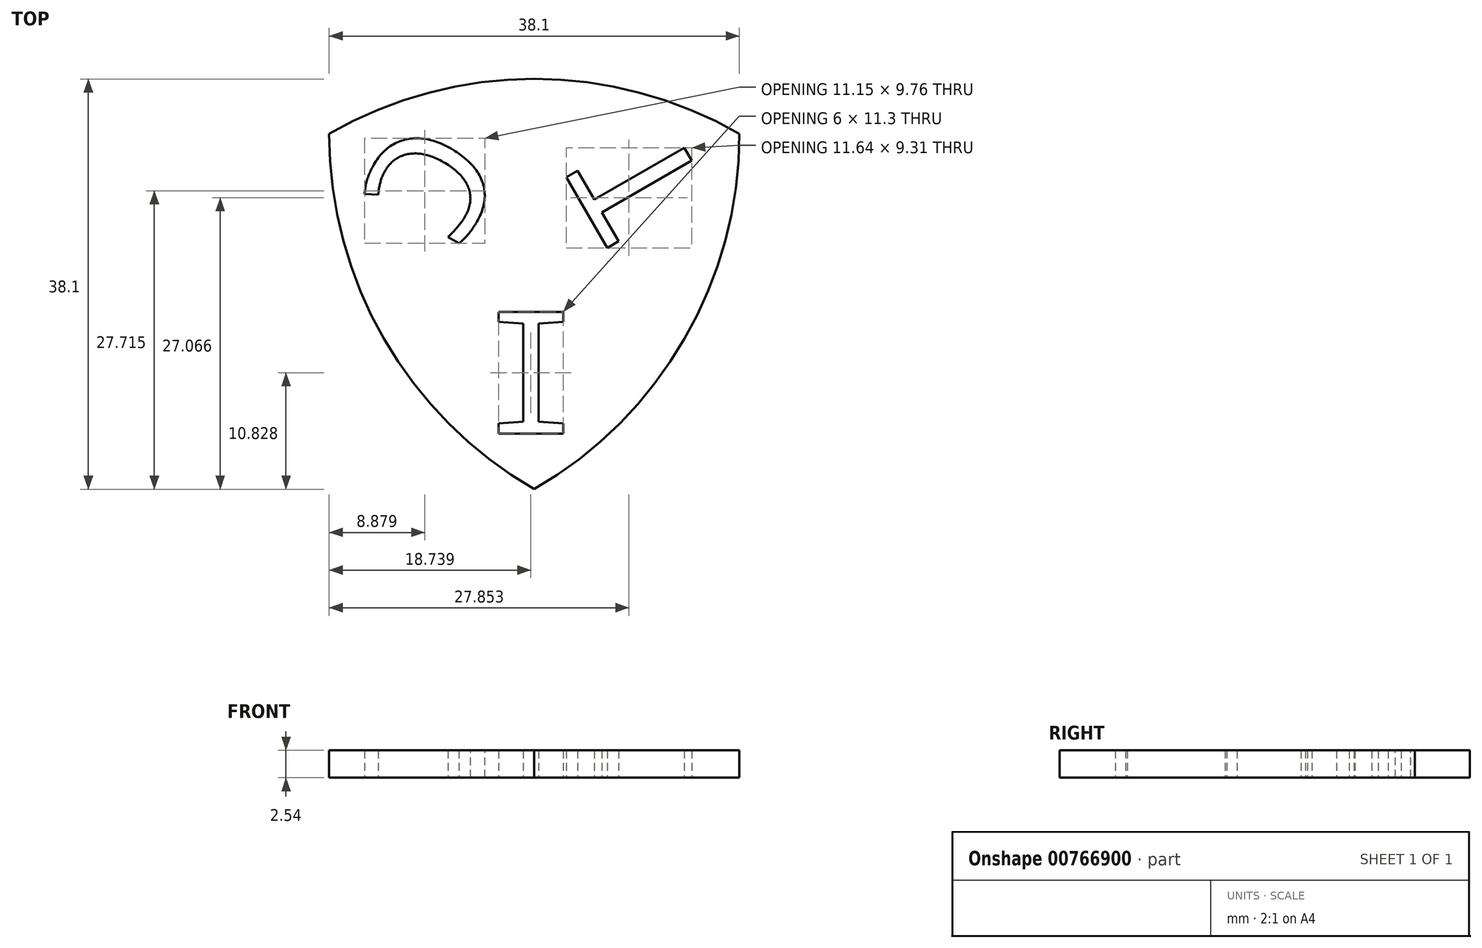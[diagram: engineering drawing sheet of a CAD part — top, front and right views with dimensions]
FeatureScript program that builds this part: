
annotation { "Feature Type Name" : "Feature", "Feature Type Description" : "" }
export const myFeature = defineFeature(function(context is Context, id is Id, definition is map)
    precondition{}
    {
        {
            var Q0;
            Q0=qCreatedBy(makeId("Top.planeOp"),FACE);
            var sketch = newSketch(context, id + "F0", { "sketchPlane" : qUnion([Q0])});
            skCircle(sketch, "E0", {"center": v(0, 0) * mm, "radius": 38.1 * mm});
            skSolve(sketch);
        }
        {
            var Q0;
            Q0=qCreatedBy(makeId("Top.planeOp"),FACE);
            var sketch = newSketch(context, id + "F1", { "sketchPlane" : qUnion([Q0])});
            skCircle(sketch, "E1", {"center": v(-38.1, 0) * mm, "radius": 38.1 * mm});
            skSolve(sketch);
        }
        {
            var Q0;
            Q0=qCreatedBy(makeId("Top.planeOp"),FACE);
            var sketch = newSketch(context, id + "F2", { "sketchPlane" : qUnion([Q0])});
            skCircle(sketch, "E2", {"center": v(-19.05, -33) * mm, "radius": 38.1 * mm});
            skSolve(sketch);
        }
        {
            var Q0;
            Q0=makeQuery(id+"F0.imprint","IMPRINT",FACE,{"disambiguationData":[TD([[makeQuery(id+"F0.imprint","IMPRINT",EDGE,{"derivedFrom":sQuery(id+"F0.wireOp",EDGE,"E0")}),1.0]])]});
            extrude(context, id + "F3", {"entities" : qUnion([Q0]), "depth" : 2.54 * mm, "offsetDistance" : 25.4 * mm});
        }
        {
            var Q0;
            Q0=makeQuery(id+"F1.imprint","IMPRINT",FACE,{"disambiguationData":[TD([[makeQuery(id+"F1.imprint","IMPRINT",EDGE,{"derivedFrom":sQuery(id+"F1.wireOp",EDGE,"E1")}),1.0]])]});
            extrude(context, id + "F4", {"entities" : qUnion([Q0]), "depth" : 2.54 * mm, "offsetDistance" : 25.4 * mm});
        }
        {
            var Q0;
            Q0=makeQuery(id+"F2.imprint","IMPRINT",FACE,{"disambiguationData":[TD([[makeQuery(id+"F2.imprint","IMPRINT",EDGE,{"derivedFrom":sQuery(id+"F2.wireOp",EDGE,"E2")}),1.0]])]});
            extrude(context, id + "F5", {"entities" : qUnion([Q0]), "depth" : 2.54 * mm, "offsetDistance" : 25.4 * mm});
        }
        {
            var Q0;
            Q0=makeQuery(id+"F4.opExtrude","SWEPT_BODY",BODY,{"disambiguationData":[OSD([sQuery(id+"F1.wireOp",EDGE,"E1")])]});
            var Q1;
            Q1=makeQuery(id+"F3.opExtrude","SWEPT_BODY",BODY,{"disambiguationData":[OSD([sQuery(id+"F0.wireOp",EDGE,"E0")])]});
            var Q2;
            Q2=makeQuery(id+"F5.opExtrude","SWEPT_BODY",BODY,{"disambiguationData":[OSD([sQuery(id+"F2.wireOp",EDGE,"E2")])]});
            booleanBodies(context, id + "F6", {"operationType" : BooleanOperationType.INTERSECTION, "tools" : qUnion([Q0, Q1, Q2])});
        }
        {
            var Q0;
            Q0=makeQuery(id+"F4.opExtrude","CAP_FACE",FACE,{"disambiguationData":[OSD([sQuery(id+"F1.wireOp",EDGE,"E1")])],"isStart":true});
            var sketch = newSketch(context, id + "F7", { "sketchPlane" : qUnion([Q0])});
            skText(sketch, "E3", { "text": "T", "fontName": "DroidSansMono.ttf"});
            skText(sketch, "E4", { "text": "I", "fontName": "DroidSansMono.ttf"});
            skText(sketch, "E5", { "text": "C", "fontName": "DroidSansMono.ttf"});
            const initialGuessF7  = {"E3": [-0.00705, -0.00206, 0.5, 0.86603, 0.01094], "E4": [-0.0241, 0.01652, 1, 0, 0.0114], "E5": [-0.0217, 0.00322, -0.5, 0.86603, 0.01073]};
            skSetInitialGuess(sketch, initialGuessF7);
            skSolve(sketch);
        }
        {
            var Q0;
            Q0 = qSketchRegion(id + "F7", true);
            extrude(context, id + "F8", {"entities" : qUnion([Q0]), "depth" : -2.54 * mm, "offsetDistance" : 25.4 * mm});
        }
        {
            var Q0;
            Q0=makeQuery(id+"F8.opExtrude","SWEPT_BODY",BODY,{"disambiguationData":[OSD([sQuery(id+"F7.wireOp",EDGE,"E3.sketch_text.stroke-0"),sQuery(id+"F7.wireOp",EDGE,"E3.sketch_text.stroke-1"),sQuery(id+"F7.wireOp",EDGE,"E3.sketch_text.stroke-2"),sQuery(id+"F7.wireOp",EDGE,"E3.sketch_text.stroke-3"),sQuery(id+"F7.wireOp",EDGE,"E3.sketch_text.stroke-4"),sQuery(id+"F7.wireOp",EDGE,"E3.sketch_text.stroke-5"),sQuery(id+"F7.wireOp",EDGE,"E3.sketch_text.stroke-6"),sQuery(id+"F7.wireOp",EDGE,"E3.sketch_text.stroke-7")])]});
            var Q1;
            Q1=makeQuery(id+"F8.opExtrude","SWEPT_BODY",BODY,{"disambiguationData":[OSD([sQuery(id+"F7.wireOp",EDGE,"E4.sketch_text.stroke-0"),sQuery(id+"F7.wireOp",EDGE,"E4.sketch_text.stroke-1"),sQuery(id+"F7.wireOp",EDGE,"E4.sketch_text.stroke-2"),sQuery(id+"F7.wireOp",EDGE,"E4.sketch_text.stroke-3"),sQuery(id+"F7.wireOp",EDGE,"E4.sketch_text.stroke-4"),sQuery(id+"F7.wireOp",EDGE,"E4.sketch_text.stroke-5"),sQuery(id+"F7.wireOp",EDGE,"E4.sketch_text.stroke-6"),sQuery(id+"F7.wireOp",EDGE,"E4.sketch_text.stroke-7"),sQuery(id+"F7.wireOp",EDGE,"E4.sketch_text.stroke-8"),sQuery(id+"F7.wireOp",EDGE,"E4.sketch_text.stroke-9"),sQuery(id+"F7.wireOp",EDGE,"E4.sketch_text.stroke-10"),sQuery(id+"F7.wireOp",EDGE,"E4.sketch_text.stroke-11")])]});
            var Q2;
            Q2=makeQuery(id+"F8.opExtrude","SWEPT_BODY",BODY,{"disambiguationData":[OSD([sQuery(id+"F7.wireOp",EDGE,"E5.sketch_text.stroke-0"),sQuery(id+"F7.wireOp",EDGE,"E5.sketch_text.stroke-1"),sQuery(id+"F7.wireOp",EDGE,"E5.sketch_text.stroke-2"),sQuery(id+"F7.wireOp",EDGE,"E5.sketch_text.stroke-3"),sQuery(id+"F7.wireOp",EDGE,"E5.sketch_text.stroke-4"),sQuery(id+"F7.wireOp",EDGE,"E5.sketch_text.stroke-5"),sQuery(id+"F7.wireOp",EDGE,"E5.sketch_text.stroke-6"),sQuery(id+"F7.wireOp",EDGE,"E5.sketch_text.stroke-7"),sQuery(id+"F7.wireOp",EDGE,"E5.sketch_text.stroke-8"),sQuery(id+"F7.wireOp",EDGE,"E5.sketch_text.stroke-9"),sQuery(id+"F7.wireOp",EDGE,"E5.sketch_text.stroke-10"),sQuery(id+"F7.wireOp",EDGE,"E5.sketch_text.stroke-11"),sQuery(id+"F7.wireOp",EDGE,"E5.sketch_text.stroke-12"),sQuery(id+"F7.wireOp",EDGE,"E5.sketch_text.stroke-13")])]});
            var Q3;
            Q3=makeQuery(id+"F6.opBoolean","INTERSECT",BODY,{"derivedFrom":[makeQuery(id+"F3.opExtrude","SWEPT_BODY",BODY,{"disambiguationData":[OSD([sQuery(id+"F0.wireOp",EDGE,"E0")])]}),makeQuery(id+"F4.opExtrude","SWEPT_BODY",BODY,{"disambiguationData":[OSD([sQuery(id+"F1.wireOp",EDGE,"E1")])]}),makeQuery(id+"F5.opExtrude","SWEPT_BODY",BODY,{"disambiguationData":[OSD([sQuery(id+"F2.wireOp",EDGE,"E2")])]})]});
            booleanBodies(context, id + "F9", {"operationType" : BooleanOperationType.SUBTRACTION, "tools" : qUnion([Q0, Q1, Q2]), "targets" : qUnion([Q3])});
        }
    });
